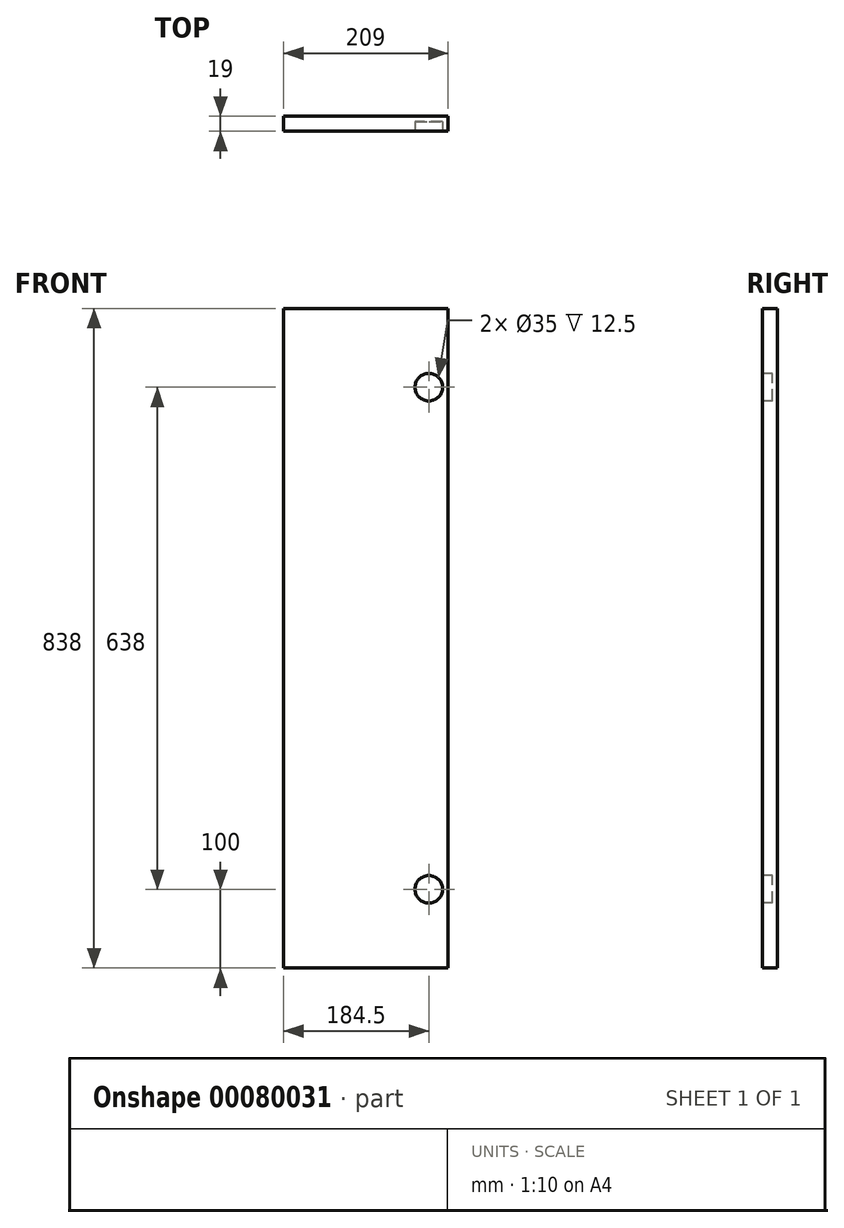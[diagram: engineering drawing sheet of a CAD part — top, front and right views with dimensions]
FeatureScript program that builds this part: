
annotation { "Feature Type Name" : "Feature", "Feature Type Description" : "" }
export const myFeature = defineFeature(function(context is Context, id is Id, definition is map)
    precondition{}
    {
        {
            var Q0;
            Q0=qCreatedBy(makeId("Front.planeOp"),FACE);
            var sketch = newSketch(context, id + "F0", { "sketchPlane" : qUnion([Q0])});
            skLineSegment(sketch, "E0.bottom", {"start": v(0, 0) * mm, "end": v(209, 0) * mm});
            skLineSegment(sketch, "E0.top", {"start": v(0, -838) * mm, "end": v(209, -838) * mm});
            skLineSegment(sketch, "E0.left", {"start": v(0, 0) * mm, "end": v(0, -838) * mm});
            skLineSegment(sketch, "E0.right", {"start": v(209, 0) * mm, "end": v(209, -838) * mm});
            skSolve(sketch);
        }
        {
            var Q0;
            Q0=makeQuery(id+"F0.imprint","IMPRINT",FACE,{"disambiguationData":[TD([[makeQuery(id+"F0.imprint","IMPRINT",EDGE,{"derivedFrom":sQuery(id+"F0.wireOp",EDGE,"E0.bottom")}),-1.0]])]});
            extrude(context, id + "F1", {"entities" : qUnion([Q0]), "depth" : 19 * mm});
        }
        {
            var Q0;
            Q0=makeQuery(id+"F1.opExtrude","CAP_FACE",FACE,{"disambiguationData":[OSD([sQuery(id+"F0.wireOp",EDGE,"E0.bottom"),sQuery(id+"F0.wireOp",EDGE,"E0.top"),sQuery(id+"F0.wireOp",EDGE,"E0.left"),sQuery(id+"F0.wireOp",EDGE,"E0.right")])],"isStart":false});
            var sketch = newSketch(context, id + "F2", { "sketchPlane" : qUnion([Q0])});
            skCircle(sketch, "E1", {"center": v(184.5, -100) * mm, "radius": 17.5 * mm});
            skCircle(sketch, "E2", {"center": v(184.5, -738) * mm, "radius": 17.5 * mm});
            skSolve(sketch);
        }
        {
            var Q0;
            Q0=makeQuery(id+"F2.imprint","IMPRINT",FACE,{"disambiguationData":[TD([[makeQuery(id+"F2.imprint","IMPRINT",EDGE,{"derivedFrom":sQuery(id+"F2.wireOp",EDGE,"E1")}),1.0]])]});
            var Q1;
            Q1=makeQuery(id+"F2.imprint","IMPRINT",FACE,{"disambiguationData":[TD([[makeQuery(id+"F2.imprint","IMPRINT",EDGE,{"derivedFrom":sQuery(id+"F2.wireOp",EDGE,"E2")}),1.0]])]});
            extrude(context, id + "F3", {"entities" : qUnion([Q0, Q1]), "operationType" : NewBodyOperationType.REMOVE, "oppositeDirection" : true, "depth" : 12.5 * mm});
        }
    });
